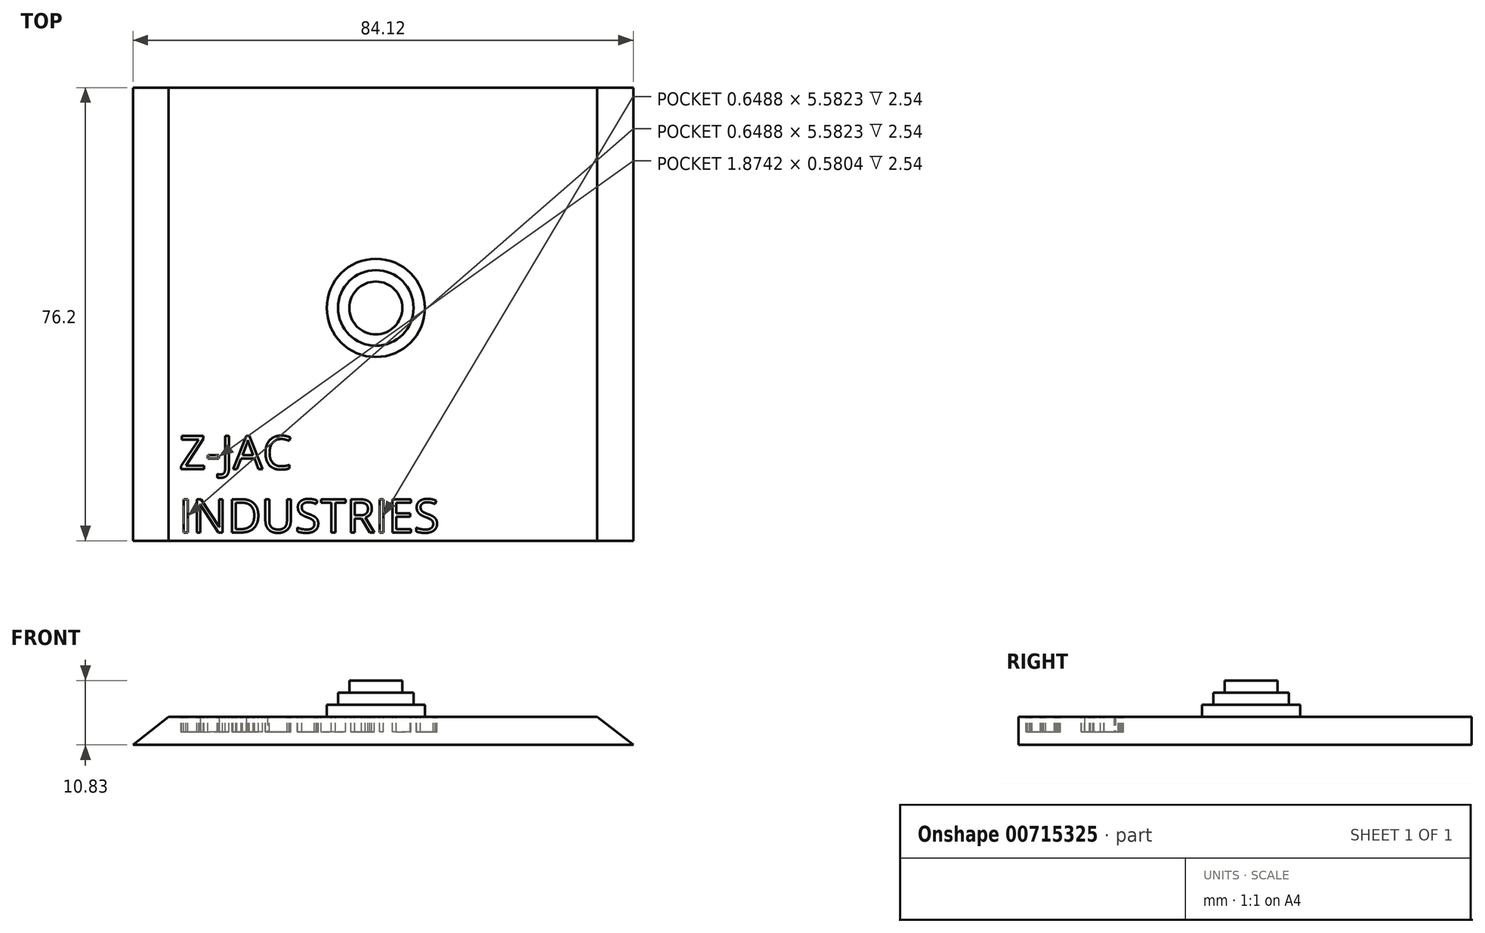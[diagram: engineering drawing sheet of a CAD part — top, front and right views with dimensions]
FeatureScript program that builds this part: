
annotation { "Feature Type Name" : "Feature", "Feature Type Description" : "" }
export const myFeature = defineFeature(function(context is Context, id is Id, definition is map)
    precondition{}
    {
        {
            var Q0;
            Q0=qCreatedBy(makeId("Front.planeOp"),FACE);
            var sketch = newSketch(context, id + "F0", { "sketchPlane" : qUnion([Q0])});
            skLineSegment(sketch, "E0", {"start": v(-2.73, 0) * mm, "end": v(-40.83, 0) * mm});
            skLineSegment(sketch, "E1", {"start": v(-40.83, 0) * mm, "end": v(-34.85, 4.73) * mm});
            skLineSegment(sketch, "E2", {"start": v(-34.85, 4.73) * mm, "end": v(37.21, 4.73) * mm});
            skLineSegment(sketch, "E3", {"start": v(37.21, 4.73) * mm, "end": v(43.3, 0) * mm});
            skLineSegment(sketch, "E4", {"start": v(43.3, 0) * mm, "end": v(-2.73, 0) * mm});
            skSolve(sketch);
        }
        {
            var Q0;
            Q0 = qSketchRegion(id + "F0", true);
            extrude(context, id + "F1", {"entities" : qUnion([Q0]), "depth" : 76.2 * mm, "offsetDistance" : 25.4 * mm});
        }
        {
            var Q0;
            Q0=makeQuery(id+"F1.opExtrude","SWEPT_FACE",FACE,{"disambiguationData":[OSD([sQuery(id+"F0.wireOp",EDGE,"E2")])]});
            var sketch = newSketch(context, id + "F2", { "sketchPlane" : qUnion([Q0])});
            skCircle(sketch, "E5", {"center": v(0, -37.05) * mm, "radius": 8.26 * mm});
            skSolve(sketch);
        }
        {
            var Q0;
            Q0=makeQuery(id+"F2.imprint","IMPRINT",FACE,{"disambiguationData":[TD([[makeQuery(id+"F2.imprint","IMPRINT",EDGE,{"derivedFrom":sQuery(id+"F2.wireOp",EDGE,"E5")}),-1.0]])]});
            var sketch = newSketch(context, id + "F3", { "sketchPlane" : qUnion([Q0])});
            skSolve(sketch);
        }
        {
            var Q0;
            Q0 = qSketchRegion(id + "F3", true);
            var Q1;
            Q1=makeQuery(id+"F3.imprint","IMPRINT",FACE,{"disambiguationData":[TD([[makeQuery(id+"F3.imprint","IMPRINT",EDGE,{"derivedFrom":makeQuery(id+"F2.imprint","IMPRINT",EDGE,{"derivedFrom":sQuery(id+"F2.wireOp",EDGE,"E5")})}),1.0]])]});
            extrude(context, id + "F4", {"entities" : qUnion([Q0, Q1]), "operationType" : NewBodyOperationType.ADD, "depth" : 2.03 * mm, "offsetDistance" : 25.4 * mm});
        }
        {
            var Q0;
            Q0=makeQuery(id+"F4.opExtrude","CAP_FACE",FACE,{"disambiguationData":[OSD([sQuery(id+"F2.wireOp",EDGE,"E5")])],"isStart":false});
            var sketch = newSketch(context, id + "F5", { "sketchPlane" : qUnion([Q0])});
            skCircle(sketch, "E6", {"center": v(0, -37.05) * mm, "radius": 6.35 * mm});
            skSolve(sketch);
        }
        {
            var Q0;
            Q0=makeQuery(id+"F5.imprint","IMPRINT",FACE,{"disambiguationData":[TD([[makeQuery(id+"F5.imprint","IMPRINT",EDGE,{"derivedFrom":sQuery(id+"F5.wireOp",EDGE,"E6")}),1.0]])]});
            extrude(context, id + "F6", {"entities" : qUnion([Q0]), "operationType" : NewBodyOperationType.ADD, "depth" : 2.03 * mm, "offsetDistance" : 25.4 * mm});
        }
        {
            var Q0;
            Q0=makeQuery(id+"F6.opExtrude","CAP_FACE",FACE,{"disambiguationData":[OSD([sQuery(id+"F5.wireOp",EDGE,"E6")])],"isStart":false});
            var sketch = newSketch(context, id + "F7", { "sketchPlane" : qUnion([Q0])});
            skCircle(sketch, "E7", {"center": v(0, -37.05) * mm, "radius": 4.45 * mm});
            skSolve(sketch);
        }
        {
            var Q0;
            Q0=makeQuery(id+"F7.imprint","IMPRINT",FACE,{"disambiguationData":[TD([[makeQuery(id+"F7.imprint","IMPRINT",EDGE,{"derivedFrom":sQuery(id+"F7.wireOp",EDGE,"E7")}),1.0]])]});
            extrude(context, id + "F8", {"entities" : qUnion([Q0]), "operationType" : NewBodyOperationType.ADD, "depth" : 2.03 * mm, "offsetDistance" : 25.4 * mm});
        }
        {
            var Q0;
            Q0=makeQuery(id+"F2.imprint","IMPRINT",FACE,{"disambiguationData":[TD([[makeQuery(id+"F2.imprint","IMPRINT",EDGE,{"derivedFrom":sQuery(id+"F2.wireOp",EDGE,"E5")}),-1.0]])]});
            var sketch = newSketch(context, id + "F9", { "sketchPlane" : qUnion([Q0])});
            skText(sketch, "E8", { "text": "Z-JAC\nINDUSTRIES", "fontName": "OpenSans-Regular.ttf"});
            const initialGuessF9  = {"E8": [-0.03306, -0.06417, 1, 0, 0.00563]};
            skSetInitialGuess(sketch, initialGuessF9);
            skSolve(sketch);
        }
        {
            var Q0;
            Q0 = qSketchRegion(id + "F9", true);
            extrude(context, id + "F10", {"entities" : qUnion([Q0]), "operationType" : NewBodyOperationType.REMOVE, "oppositeDirection" : true, "depth" : 2.54 * mm, "offsetDistance" : 25.4 * mm});
        }
    });
